# Revit family: S-757
name_source: partatom
category: Plumbing Fixtures
revit_build: Autodesk Revit 2015 (Build: 20140606_1530(x64)
units: mm (PartAtom-declared; Revit-internal decimal feet)

## types (12) — shared parameters
B = 52 mm
Manufacturer = Jimten
Model = S-757
Type Comments = COMPATIBLE WITH VISIBLE OR THIN FRAMES
URL = http://www.jimten.com

## per-type parameters (varying)
| type | A | Description | Grid | Material | Reference | Size |
| 50x350mm_CRYSTAL BLACK | 340 mm  [stored 1.11549 ft] | CHANNEL GRID, BLACK GLASS, FOR CHANNELS WIDTH 50 | Tempered glass (Black) | Tempered glass (Black) | 13533 | 350mm x 50mm |
| 50x550mm_CRYSTAL BLACK | 540 mm  [stored 1.77165 ft] | CHANNEL GRID, BLACK GLASS, FOR CHANNELS WIDTH 50 | Tempered glass (Black) | Tempered glass (Black) | 13553 | 550mm x 50mm |
| 50x650mm_CRYSTAL BLACK | 640 mm  [stored 2.09974 ft] | CHANNEL GRID, BLACK GLASS, FOR CHANNELS WIDTH 50 | Tempered glass (Black) | Tempered glass (Black) | 13563 | 650mm x 50mm |
| 50x750mm_CRYSTAL BLACK | 740 mm  [stored 2.42782 ft] | CHANNEL GRID, BLACK GLASS, FOR CHANNELS WIDTH 50 | Tempered glass (Black) | Tempered glass (Black) | 13573 | 750mm x 50mm |
| 50x850mm_CRYSTAL BLACK | 840 mm  [stored 2.75591 ft] | CHANNEL GRID, BLACK GLASS, FOR CHANNELS WIDTH 50 | Tempered glass (Black) | Tempered glass (Black) | 13583 | 850mm x 50mm |
| 50x950mm_CRYSTAL BLACK | 940 mm  [stored 3.08399 ft] | CHANNEL GRID, BLACK GLASS, FOR CHANNELS WIDTH 50 | Tempered glass (Black) | Tempered glass (Black) | 13593 | 950mm x 50mm |
| 50x350mm_CRYSTAL WHITE | 340 mm  [stored 1.11549 ft] | CHANNEL GRID, WHITE GLASS, FOR CHANNELS WIDTH 50 | Tempered glass (White) | Tempered glass (White) | 13534 | 350mm x 50mm |
| 50x550mm_CRYSTAL WHITE | 540 mm  [stored 1.77165 ft] | CHANNEL GRID, WHITE GLASS, FOR CHANNELS WIDTH 50 | Tempered glass (White) | Tempered glass (White) | 13554 | 550mm x 50mm |
| 50x650mm_CRYSTAL WHITE | 640 mm  [stored 2.09974 ft] | CHANNEL GRID, WHITE GLASS, FOR CHANNELS WIDTH 50 | Tempered glass (White) | Tempered glass (White) | 13564 | 650mm x 50mm |
| 50x750mm_CRYSTAL WHITE | 740 mm  [stored 2.42782 ft] | CHANNEL GRID, WHITE GLASS, FOR CHANNELS WIDTH 50 | Tempered glass (White) | Tempered glass (White) | 13574 | 750mm x 50mm |
| 50x850mm_CRYSTAL WHITE | 840 mm  [stored 2.75591 ft] | CHANNEL GRID, WHITE GLASS, FOR CHANNELS WIDTH 50 | Tempered glass (White) | Tempered glass (White) | 13584 | 850mm x 50mm |
| 50x950mm_CRYSTAL WHITE | 940 mm  [stored 3.08399 ft] | CHANNEL GRID, WHITE GLASS, FOR CHANNELS WIDTH 50 | Tempered glass (White) | Tempered glass (White) | 13594 | 950mm x 50 mm |

note: [stored X ft] marks values corroborated as IEEE doubles in the binary element streams (Revit-internal decimal feet)

## geometry (parser evidence)
native form markers: Blend x3, Sweep x3
no freeform markers — native parametric forms only
